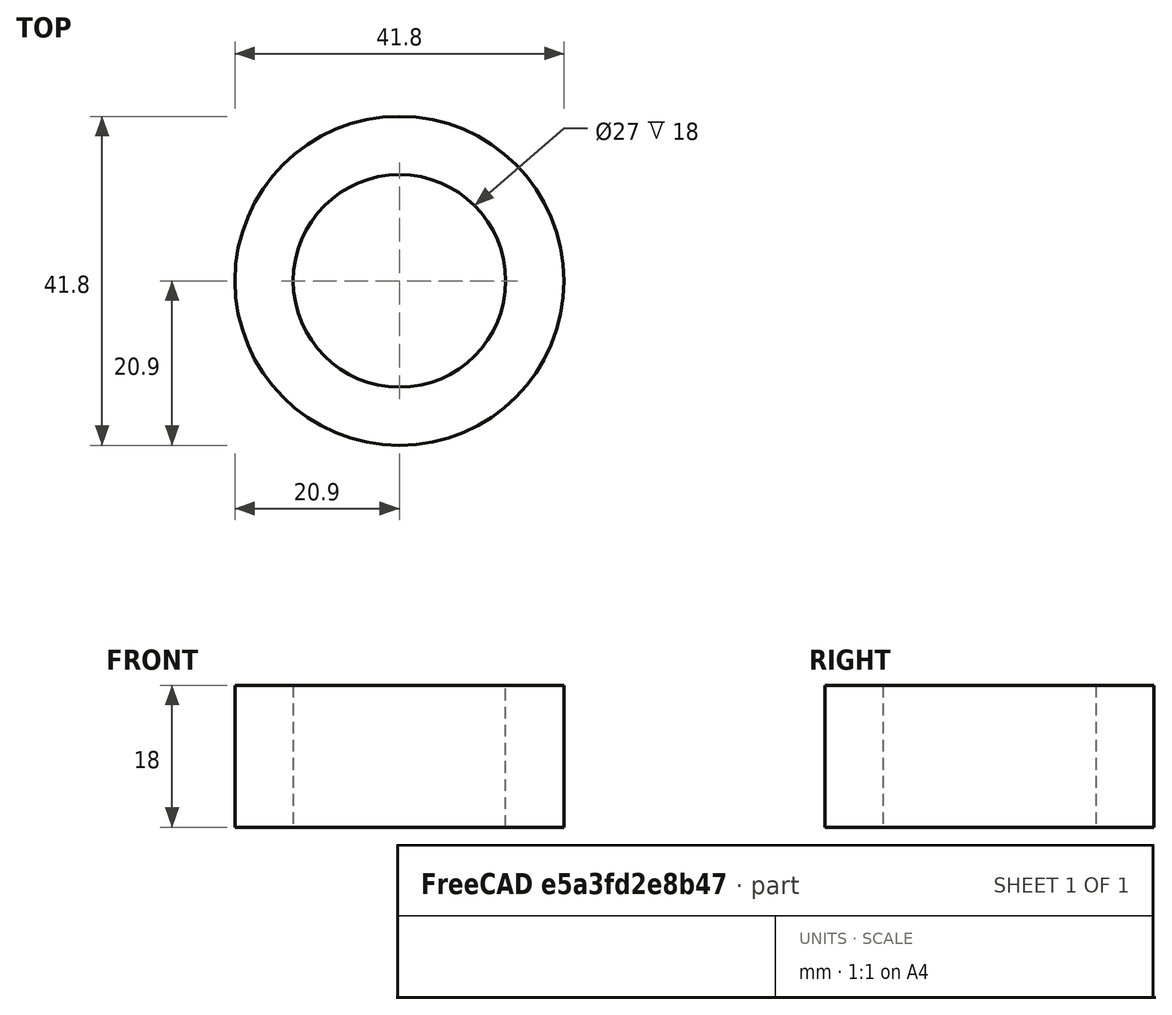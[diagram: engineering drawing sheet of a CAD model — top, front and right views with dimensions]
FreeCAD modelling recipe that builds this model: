
FCSTD DOCUMENT  (FreeCAD 0.19R24291 (Git))
Label: UTASensorAdapter
License: All rights reserved
LicenseURL: http://en.wikipedia.org/wiki/All_rights_reserved
objects: Sketcher::SketchObject×1, PartDesign::Pad×1, PartDesign::Body×1
note: 4 computed .brp shape members not serialized (recipe doc carries the construction recipe); baked Part::Feature solids carry a one-line shape summary decoded from their .brp

FEATURE [Sketcher::SketchObject] Sketch
  FullyConstrained = true
  MapMode = 5
  Support = -> [XY_Plane]
  sketch-geometry (2):
    g0: Circle CenterX=0 CenterY=0 CenterZ=0 NormalX=0 NormalY=0 NormalZ=1 AngleXU=0 Radius=20.9
    g1: Circle CenterX=0 CenterY=0 CenterZ=0 NormalX=0 NormalY=0 NormalZ=1 AngleXU=0 Radius=13.5
  constraints (4):
    c: Coincident(g0,g-1)
    c: Coincident(g1,g0)
    c: Radius(g1) = 13.5
    c: Radius(g0) = 20.9
FEATURE [PartDesign::Pad] Pad
  Direction = (1,1,1)
  Length = 18
  Length2 = 100
  Profile = -> Sketch
  Type = 0
FEATURE [PartDesign::Body] Body
  Group = -> [Sketch,Pad]
  Origin = -> Origin
  Tip = -> Pad
